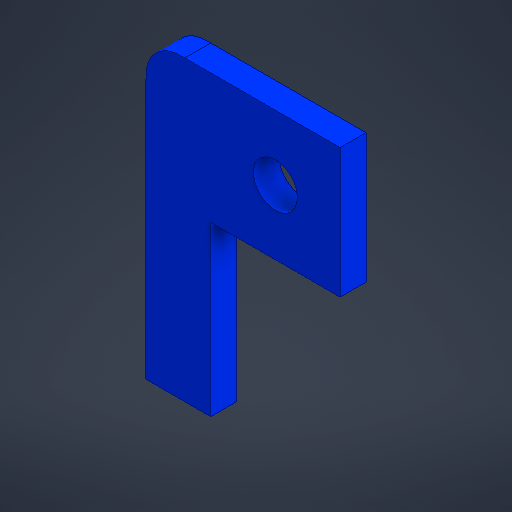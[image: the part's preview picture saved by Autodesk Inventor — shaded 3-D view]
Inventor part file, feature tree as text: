
AUTODESK INVENTOR PART (.ipt)
format: ipt  version: 2025.1 (Build 291241000, 241)  size: 474,112 bytes
history: native  units: mm
features: extrude x1, fillet x1, sketch x1
ambient origin geometry x8: Origin, YZ Plane, XZ Plane, XY Plane, X Axis, Y Axis, Z Axis, Center Point
bodies: Solid1 (feature_tree)
feature tree (3):
  extrude  "Extrusion1"  Depth=3.0mm
  fillet  "Fillet1"  Radius=23.0mm
  sketch  "Sketch1"  dims[d8=2.0mm d9=0.0mm d13=3.0mm d14=23.0mm d15=15.0mm d16=10.0mm d17=10.0mm d18=3.4mm d19=5.0mm d20=5.0mm d21=0.0mm d22=0.0mm d23=0.0mm d24=0.0mm]
